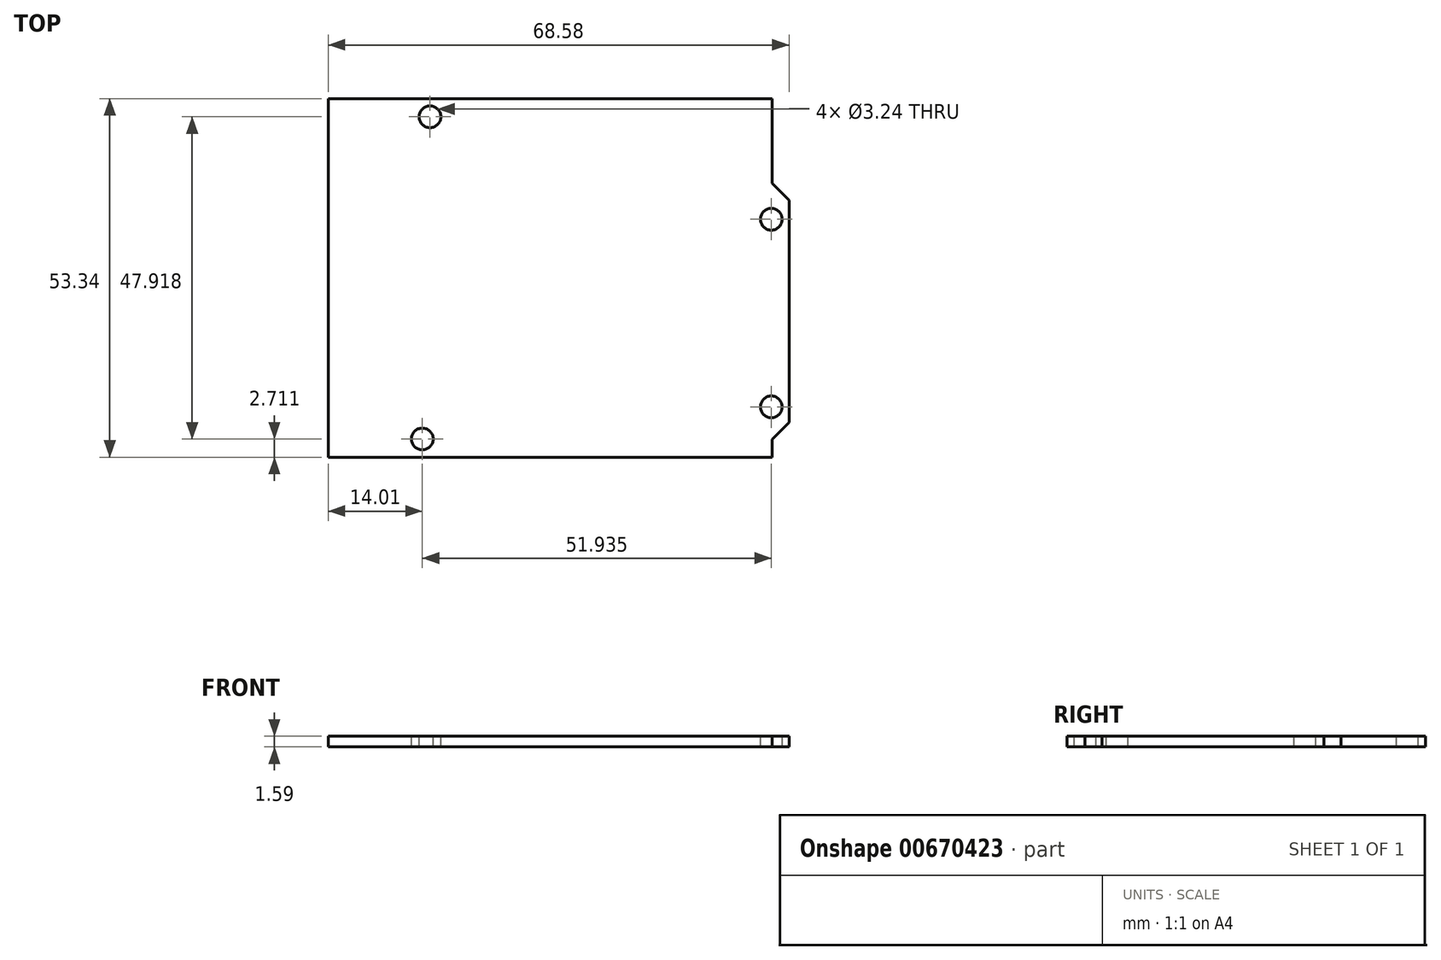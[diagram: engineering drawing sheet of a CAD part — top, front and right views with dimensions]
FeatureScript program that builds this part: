
annotation { "Feature Type Name" : "Feature", "Feature Type Description" : "" }
export const myFeature = defineFeature(function(context is Context, id is Id, definition is map)
    precondition{}
    {
        {
            var Q0;
            Q0=qCreatedBy(makeId("Top.planeOp"),FACE);
            var sketch = newSketch(context, id + "F0", { "sketchPlane" : qUnion([Q0])});
            skLineSegment(sketch, "E0", {"start": v(-33.02, 26.67) * mm, "end": v(33.02, 26.67) * mm});
            skLineSegment(sketch, "E1", {"start": v(33.02, 26.67) * mm, "end": v(33.02, -26.67) * mm, "construction": true});
            skLineSegment(sketch, "E2", {"start": v(33.02, -26.67) * mm, "end": v(-33.02, -26.67) * mm});
            skLineSegment(sketch, "E3", {"start": v(-33.02, -26.67) * mm, "end": v(-33.02, 26.67) * mm});
            skLineSegment(sketch, "E4", {"start": v(33.02, -24) * mm, "end": v(35.56, -21.46) * mm});
            skLineSegment(sketch, "E5", {"start": v(35.56, -21.46) * mm, "end": v(35.56, 11.56) * mm});
            skLineSegment(sketch, "E6", {"start": v(35.56, 11.56) * mm, "end": v(33.02, 14.1) * mm});
            skLineSegment(sketch, "E7", {"start": v(0, 0) * mm, "end": v(-33.02, 0) * mm, "construction": true});
            skLineSegment(sketch, "E8", {"start": v(0, 0) * mm, "end": v(0, 26.67) * mm, "construction": true});
            skLineSegment(sketch, "E9", {"start": v(33.02, 26.67) * mm, "end": v(33.02, 14.1) * mm});
            skLineSegment(sketch, "E10", {"start": v(33.02, -26.67) * mm, "end": v(33.02, -24) * mm});
            skSolve(sketch);
        }
        {
            var Q0;
            Q0 = qSketchRegion(id + "F0", true);
            extrude(context, id + "F1", {"entities" : qUnion([Q0]), "depth" : 1.59 * mm, "offsetDistance" : 25 * mm});
        }
        {
            var Q0;
            Q0=makeQuery(id+"F1.opExtrude","CAP_FACE",FACE,{"disambiguationData":[OSD([sQuery(id+"F0.wireOp",EDGE,"E0"),sQuery(id+"F0.wireOp",EDGE,"E2"),sQuery(id+"F0.wireOp",EDGE,"E3"),sQuery(id+"F0.wireOp",EDGE,"E4"),sQuery(id+"F0.wireOp",EDGE,"E5"),sQuery(id+"F0.wireOp",EDGE,"E6"),sQuery(id+"F0.wireOp",EDGE,"E9"),sQuery(id+"F0.wireOp",EDGE,"E10")])],"isStart":false});
            var sketch = newSketch(context, id + "F2", { "sketchPlane" : qUnion([Q0])});
            skCircle(sketch, "E11", {"center": v(-17.86, 23.96) * mm, "radius": 1.62 * mm});
            skCircle(sketch, "E12", {"center": v(32.93, 8.72) * mm, "radius": 1.62 * mm});
            skCircle(sketch, "E13", {"center": v(32.93, -19.19) * mm, "radius": 1.62 * mm});
            skCircle(sketch, "E14", {"center": v(-19.01, -23.96) * mm, "radius": 1.62 * mm});
            skSolve(sketch);
        }
        {
            var Q0;
            Q0 = qSketchRegion(id + "F2", true);
            extrude(context, id + "F3", {"entities" : qUnion([Q0]), "operationType" : NewBodyOperationType.REMOVE, "endBound" : BoundingType.THROUGH_ALL, "oppositeDirection" : true, "depth" : 25 * mm, "offsetDistance" : 25 * mm});
        }
    });
